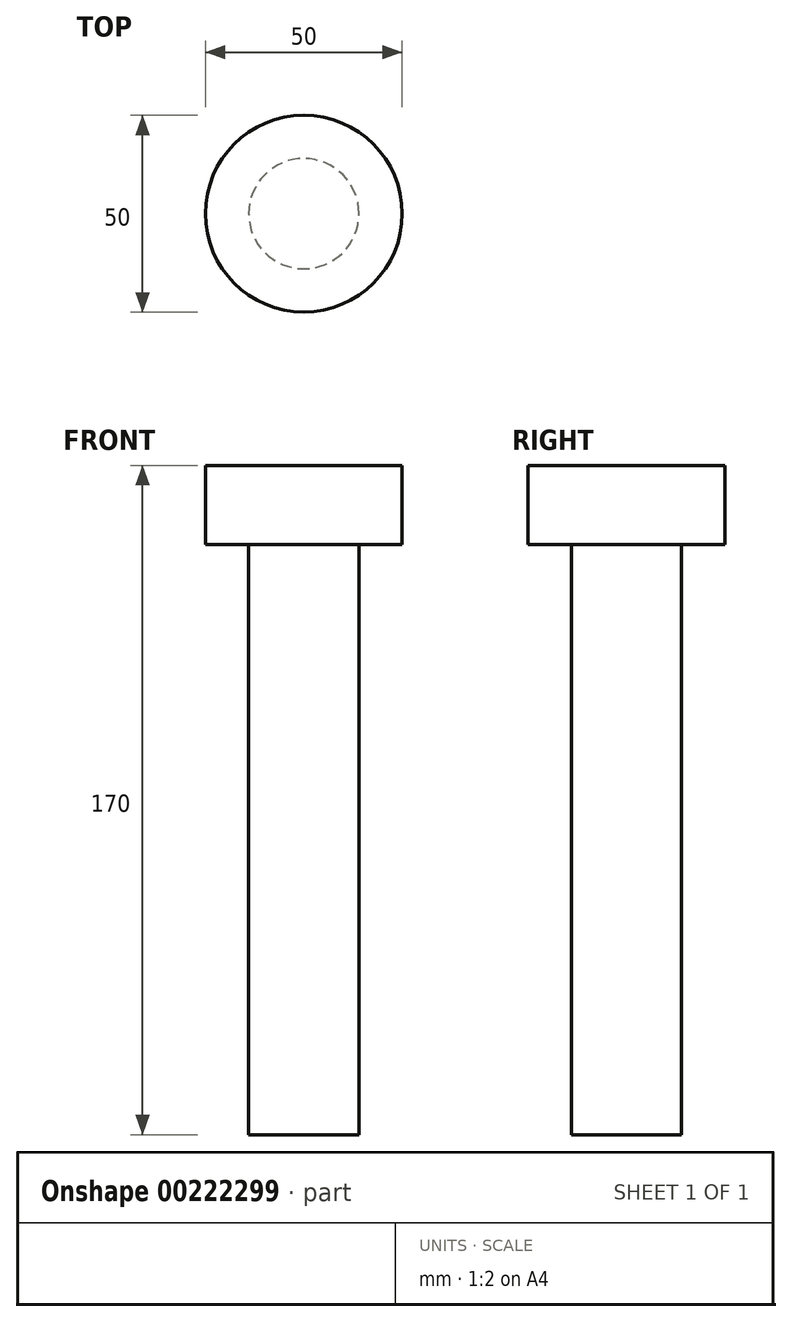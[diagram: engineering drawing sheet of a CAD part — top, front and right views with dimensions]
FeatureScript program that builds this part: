
annotation { "Feature Type Name" : "Feature", "Feature Type Description" : "" }
export const myFeature = defineFeature(function(context is Context, id is Id, definition is map)
    precondition{}
    {
        {
            var Q0;
            Q0=qCreatedBy(makeId("Top.planeOp"),FACE);
            var sketch = newSketch(context, id + "F0", { "sketchPlane" : qUnion([Q0])});
            skCircle(sketch, "E0", {"center": v(0, 0) * mm, "radius": 14 * mm});
            skSolve(sketch);
        }
        {
            var Q0;
            Q0 = qSketchRegion(id + "F0", true);
            extrude(context, id + "F1", {"entities" : qUnion([Q0]), "oppositeDirection" : true, "depth" : 150 * mm, "offsetDistance" : 25 * mm});
        }
        {
            var Q0;
            Q0=makeQuery(id+"F1.opExtrude","CAP_FACE",FACE,{"disambiguationData":[OSD([sQuery(id+"F0.wireOp",EDGE,"E0")])],"isStart":true});
            var sketch = newSketch(context, id + "F2", { "sketchPlane" : qUnion([Q0])});
            skCircle(sketch, "E1", {"center": v(0, 0) * mm, "radius": 25 * mm});
            skSolve(sketch);
        }
        {
            var Q0;
            Q0 = qSketchRegion(id + "F2", true);
            extrude(context, id + "F3", {"entities" : qUnion([Q0]), "operationType" : NewBodyOperationType.ADD, "depth" : 20 * mm, "offsetDistance" : 25 * mm});
        }
    });
